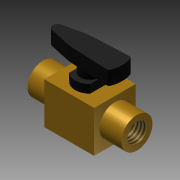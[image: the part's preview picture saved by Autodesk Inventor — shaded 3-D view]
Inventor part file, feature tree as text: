
AUTODESK INVENTOR PART (.ipt)
format: ipt  version: 2011 (Build 150239000, 239)  size: 163,328 bytes
history: native  units: mm (DEFAULTED — no unit token found)
features: extrude x10, sketch x10, projected_geometry x5, thread x2
ambient origin geometry x8: Origin, YZ Plane, XZ Plane, XY Plane, X Axis, Y Axis, Z Axis, Center Point
bodies: Solid1 (feature_tree)
feature tree (27):
  extrude  "Extrusion1"  Depth=22.86mm
  extrude  "Extrusion2"  Depth=14.224mm
  extrude  "Extrusion3"  Depth=14.224mm
  extrude  "Extrusion4"  Depth=3.81mm TaperAngle=0.0deg
  extrude  "Extrusion5"  Depth=6.35mm TaperAngle=0.0deg
  extrude  "Extrusion6"  Depth=9.525mm TaperAngle=0.0deg
  extrude  "Extrusion7"  Depth=3.175mm
  extrude  "Extrusion9"  Depth=25.4mm TaperAngle=0.0deg
  thread  "Thread1"  [1 undecoded]
  thread  "Thread2"  [1 undecoded]
  extrude  "Extrusion10"  [1 undecoded]
  sketch  "Sketch1"  dims[d0=19.05mm d1=22.86mm]
  sketch  "Sketch2"  dims[d2=19.05mm d3=0.0mm d4=14.224mm]
  projected_geometry  "Projected Loop1"
  sketch  "Sketch3"  dims[d5=10.16mm d6=0.0mm d7=14.224mm]
  projected_geometry  "Projected Loop2"
  sketch  "Sketch4"  dims[d8=10.16mm d9=0.0mm d10=3.81mm d11=0.0mm]
  projected_geometry  "Projected Loop3"
  sketch  "Sketch5"  dims[d12=10.16mm d13=0.0mm d14=6.35mm d15=0.0mm]
  projected_geometry  "Projected Loop4"
  sketch  "Sketch6"  dims[d16=8.89mm d17=9.525mm d18=0.0mm]
  projected_geometry  "Projected Loop5"
  sketch  "Sketch7"  dims[d19=8.89mm d21=0.0mm d22=9.525mm d23=3.175mm]
  sketch  "Sketch8"  dims[d24=71.4502mm d25=0.0mm d26=25.4mm d27=0.0mm d28=25.4mm d29=0.0mm d30=1.6002mm d31=0.0mm]
  sketch  "Sketch9"
  sketch  "Sketch10"
  extrude  "Extrusion8"  [1 undecoded]
note: 4 required parameter values undecoded (feature->parameter linkage not recoverable at this tier; creation-order binding heuristic only, values carry confidence <= 0.55)
